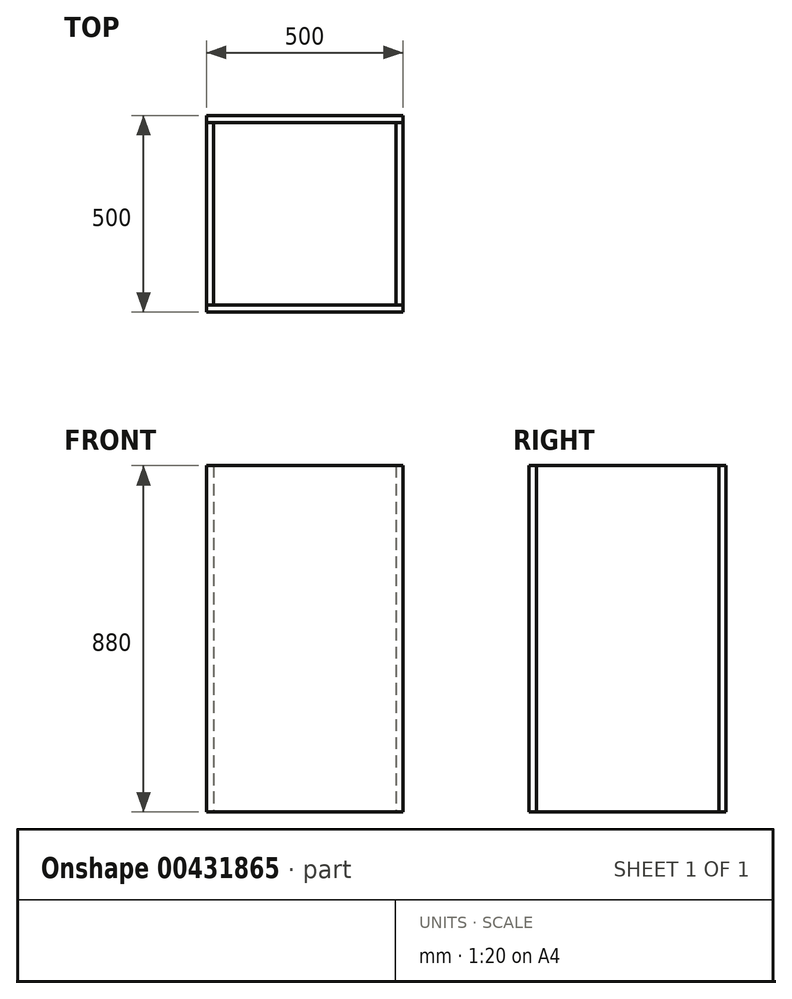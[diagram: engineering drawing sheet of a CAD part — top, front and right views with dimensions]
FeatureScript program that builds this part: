
annotation { "Feature Type Name" : "Feature", "Feature Type Description" : "" }
export const myFeature = defineFeature(function(context is Context, id is Id, definition is map)
    precondition{}
    {
        {
            var Q0;
            Q0=qCreatedBy(makeId("Top.planeOp"),FACE);
            var sketch = newSketch(context, id + "F0", { "sketchPlane" : qUnion([Q0])});
            skLineSegment(sketch, "E0.bottom", {"start": v(-762.19, 438) * mm, "end": v(-262.19, 438) * mm});
            skLineSegment(sketch, "E0.top", {"start": v(-762.19, -62) * mm, "end": v(-262.19, -62) * mm});
            skLineSegment(sketch, "E0.left", {"start": v(-762.19, 438) * mm, "end": v(-762.19, -62) * mm});
            skLineSegment(sketch, "E0.right", {"start": v(-262.19, 438) * mm, "end": v(-262.19, -62) * mm});
            skLineSegment(sketch, "E1.bottom", {"start": v(-744.19, 420) * mm, "end": v(-280.19, 420) * mm});
            skLineSegment(sketch, "E1.top", {"start": v(-744.19, -44) * mm, "end": v(-280.19, -44) * mm});
            skLineSegment(sketch, "E1.left", {"start": v(-744.19, 420) * mm, "end": v(-744.19, -44) * mm});
            skLineSegment(sketch, "E1.right", {"start": v(-280.19, 420) * mm, "end": v(-280.19, -44) * mm});
            skLineSegment(sketch, "E2", {"start": v(-744.19, 420) * mm, "end": v(-762.19, 420) * mm});
            skLineSegment(sketch, "E3", {"start": v(-280.19, 420) * mm, "end": v(-262.19, 420) * mm});
            skLineSegment(sketch, "E4", {"start": v(-280.19, -44) * mm, "end": v(-262.19, -44) * mm});
            skLineSegment(sketch, "E5", {"start": v(-744.19, -44) * mm, "end": v(-762.19, -44) * mm});
            skSolve(sketch);
        }
        {
            var Q0;
            {var subQ1=sQuery(id+"F0.wireOp",EDGE,"E0.bottom");Q0=makeQuery(id+"F0.imprint","IMPRINT",FACE,{"disambiguationData":[TD([[makeQuery(id+"F0.imprint","IMPRINT",EDGE,{"derivedFrom":subQ1}),-1.0]])]});}
            var Q1;
            {var subQ1=sQuery(id+"F0.wireOp",EDGE,"E0.top");Q1=makeQuery(id+"F0.imprint","IMPRINT",FACE,{"disambiguationData":[TD([[makeQuery(id+"F0.imprint","IMPRINT",EDGE,{"derivedFrom":subQ1}),1.0]])]});}
            extrude(context, id + "F1", {"entities" : qUnion([Q0, Q1]), "depth" : 880 * mm, "offsetDistance" : 25 * mm});
        }
        {
            var Q0;
            Q0=makeQuery(id+"F0.imprint","IMPRINT",FACE,{"disambiguationData":[TD([[makeQuery(id+"F0.imprint","IMPRINT",EDGE,{"derivedFrom":sQuery(id+"F0.wireOp",EDGE,"E1.left")}),-1.0]])]});
            var Q1;
            Q1=makeQuery(id+"F0.imprint","IMPRINT",FACE,{"disambiguationData":[TD([[makeQuery(id+"F0.imprint","IMPRINT",EDGE,{"derivedFrom":sQuery(id+"F0.wireOp",EDGE,"E1.right")}),1.0]])]});
            extrude(context, id + "F2", {"entities" : qUnion([Q0, Q1]), "depth" : 880 * mm, "offsetDistance" : 25 * mm});
        }
    });
